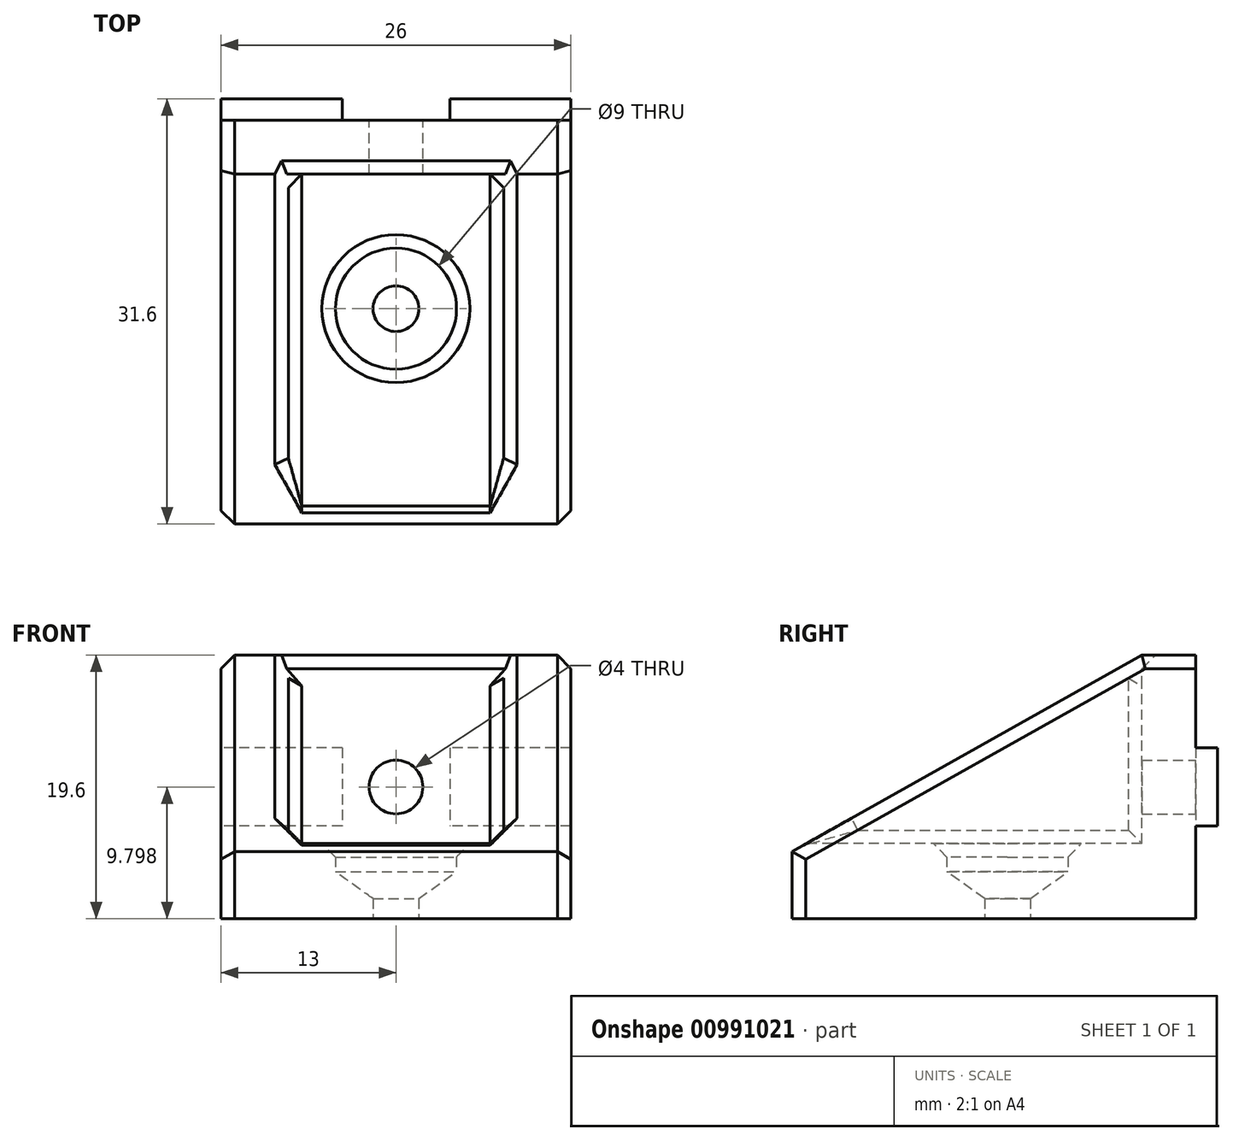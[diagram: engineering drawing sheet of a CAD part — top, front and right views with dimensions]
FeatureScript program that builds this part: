
annotation { "Feature Type Name" : "Feature", "Feature Type Description" : "" }
export const myFeature = defineFeature(function(context is Context, id is Id, definition is map)
    precondition{}
    {
        {
            var Q0;
            Q0=qCreatedBy(makeId("Right.planeOp"),FACE);
            var sketch = newSketch(context, id + "F0", { "sketchPlane" : qUnion([Q0])});
            skLineSegment(sketch, "E0", {"start": v(-34.07, -18.6) * mm, "end": v(-4.07, -18.6) * mm});
            skLineSegment(sketch, "E1", {"start": v(-4.07, -18.6) * mm, "end": v(-4.07, -11.7) * mm});
            skLineSegment(sketch, "E2", {"start": v(-4.07, -11.7) * mm, "end": v(-2.47, -11.7) * mm});
            skLineSegment(sketch, "E3", {"start": v(-2.47, -11.7) * mm, "end": v(-2.47, -5.9) * mm});
            skLineSegment(sketch, "E4", {"start": v(-2.47, -5.9) * mm, "end": v(-4.07, -5.9) * mm});
            skLineSegment(sketch, "E5", {"start": v(-4.07, -5.9) * mm, "end": v(-4.07, 1) * mm});
            skLineSegment(sketch, "E6", {"start": v(-4.07, 1) * mm, "end": v(-8.07, 1) * mm});
            skLineSegment(sketch, "E7", {"start": v(-8.07, 1) * mm, "end": v(-34.07, -13.6) * mm});
            skLineSegment(sketch, "E8", {"start": v(-34.07, -13.6) * mm, "end": v(-34.07, -18.6) * mm});
            skSolve(sketch);
        }
        {
            var Q0;
            Q0=makeQuery(id+"F0.imprint","IMPRINT",FACE,{"disambiguationData":[TD([[makeQuery(id+"F0.imprint","IMPRINT",EDGE,{"derivedFrom":sQuery(id+"F0.wireOp",EDGE,"E0")}),1.0]])]});
            var Q1;
            Q1 = qSketchRegion(id + "F2", true);
            extrude(context, id + "F1", {"entities" : qUnion([Q0, Q1]), "depth" : 26 * mm, "offsetDistance" : 25 * mm});
        }
        {
            var Q0;
            Q0=makeQuery(id+"F1.opExtrude","SWEPT_FACE",FACE,{"disambiguationData":[OSD([sQuery(id+"F0.wireOp",EDGE,"E3")])]});
            var sketch = newSketch(context, id + "F2", { "sketchPlane" : qUnion([Q0])});
            skLineSegment(sketch, "E9", {"start": v(-13, -5.9) * mm, "end": v(-13, -11.7) * mm, "construction": true});
            skCircle(sketch, "E10", {"center": v(-13, -8.8) * mm, "radius": 2 * mm});
            skSolve(sketch);
        }
        {
            var Q0;
            Q0=makeQuery(id+"F2.imprint","IMPRINT",FACE,{"disambiguationData":[TD([[makeQuery(id+"F2.imprint","IMPRINT",EDGE,{"derivedFrom":sQuery(id+"F2.wireOp",EDGE,"E10")}),1.0]])]});
            extrude(context, id + "F3", {"entities" : qUnion([Q0]), "operationType" : NewBodyOperationType.REMOVE, "endBound" : BoundingType.UP_TO_NEXT, "oppositeDirection" : true, "depth" : 25 * mm, "offsetDistance" : 25 * mm});
        }
        {
            var Q0;
            Q0=makeQuery(id+"F1.opExtrude","SWEPT_FACE",FACE,{"disambiguationData":[OSD([sQuery(id+"F0.wireOp",EDGE,"E6")])]});
            var sketch = newSketch(context, id + "F4", { "sketchPlane" : qUnion([Q0])});
            skLineSegment(sketch, "E11", {"start": v(13, -8.07) * mm, "end": v(13, -33.07) * mm, "construction": true});
            skLineSegment(sketch, "E12.bottom", {"start": v(5, -8.07) * mm, "end": v(21, -8.07) * mm});
            skLineSegment(sketch, "E12.top", {"start": v(5, -33.07) * mm, "end": v(21, -33.07) * mm});
            skLineSegment(sketch, "E12.left", {"start": v(5, -8.07) * mm, "end": v(5, -33.07) * mm});
            skLineSegment(sketch, "E12.right", {"start": v(21, -8.07) * mm, "end": v(21, -33.07) * mm});
            skSolve(sketch);
        }
        {
            var Q0;
            Q0=makeQuery(id+"F4.imprint","IMPRINT",FACE,{"disambiguationData":[TD([[makeQuery(id+"F4.imprint","IMPRINT",EDGE,{"derivedFrom":sQuery(id+"F4.wireOp",EDGE,"E12.bottom")}),1.0]])]});
            extrude(context, id + "F5", {"entities" : qUnion([Q0]), "operationType" : NewBodyOperationType.REMOVE, "oppositeDirection" : true, "depth" : 14 * mm, "offsetDistance" : 25 * mm});
        }
        {
            var Q0;
            Q0=makeQuery(id+"F1.opExtrude","SWEPT_FACE",FACE,{"disambiguationData":[OSD([sQuery(id+"F0.wireOp",EDGE,"E3")])]});
            var sketch = newSketch(context, id + "F6", { "sketchPlane" : qUnion([Q0])});
            skLineSegment(sketch, "E13", {"start": v(-13, -5.9) * mm, "end": v(-13, -11.7) * mm, "construction": true});
            skLineSegment(sketch, "E14", {"start": v(-17, -5.9) * mm, "end": v(-17, -11.7) * mm});
            skLineSegment(sketch, "E15.MirrorCS", {"start": v(-9, -5.9) * mm, "end": v(-9, -11.7) * mm});
            skSolve(sketch);
        }
        {
            var Q0;
            {var subQ0=sQuery(id+"F6.wireOp",EDGE,"E14");Q0=makeQuery(id+"F6.imprint","IMPRINT",FACE,{"disambiguationData":[TD([[makeQuery(id+"F6.imprint","IMPRINT",EDGE,{"derivedFrom":subQ0}),1.0]])]});}
            var Q1;
            Q1=makeQuery(id+"F1.opExtrude","SWEPT_FACE",FACE,{"disambiguationData":[OSD([sQuery(id+"F0.wireOp",EDGE,"E5")])]});
            extrude(context, id + "F7", {"entities" : qUnion([Q0]), "operationType" : NewBodyOperationType.REMOVE, "endBound" : BoundingType.UP_TO_SURFACE, "oppositeDirection" : true, "depth" : 25 * mm, "endBoundEntityFace" : qUnion([Q1]), "offsetDistance" : 25 * mm});
        }
        {
            var Q0;
            Q0=makeQuery(id+"F5.boolean.opBoolean","MERGE",EDGE,{"derivedFrom":[makeQuery(id+"F1.opExtrude","SWEPT_EDGE",EDGE,{"disambiguationData":[OSD([sQuery(id+"F0.wireOp",EDGE,"E6"),sQuery(id+"F0.wireOp",EDGE,"E7")])]})],"fromTools":[makeQuery(id+"F5.opExtrude","CAP_EDGE",EDGE,{"disambiguationData":[OSD([sQuery(id+"F4.wireOp",EDGE,"E12.bottom")])],"isStart":true})]});
            cPoint(context, id + "F8", {"entities" : qUnion([Q0]), "parameter" : 0.5});
        }
        {
            var Q0;
            Q0=makeQuery(id+"F5.boolean.opBoolean","INTERSECT",EDGE,{"derivedFrom":[makeQuery(id+"F1.opExtrude","SWEPT_FACE",FACE,{"disambiguationData":[OSD([sQuery(id+"F0.wireOp",EDGE,"E7")])]}),makeQuery(id+"F5.opExtrude","CAP_FACE",FACE,{"disambiguationData":[OSD([sQuery(id+"F4.wireOp",EDGE,"E12.bottom"),sQuery(id+"F4.wireOp",EDGE,"E12.top"),sQuery(id+"F4.wireOp",EDGE,"E12.left"),sQuery(id+"F4.wireOp",EDGE,"E12.right")])],"isStart":false})]});
            cPoint(context, id + "F9", {"entities" : qUnion([Q0]), "parameter" : 0.5});
        }
        {
            var Q0;
            Q0=makeQuery(id+"F5.boolean.opBoolean","COPY",EDGE,{"derivedFrom":makeQuery(id+"F5.opExtrude","CAP_EDGE",EDGE,{"disambiguationData":[OSD([sQuery(id+"F4.wireOp",EDGE,"E12.bottom")])],"isStart":false})});
            cPoint(context, id + "F10", {"entities" : qUnion([Q0]), "parameter" : 0.5});
        }
        {
            var Q0;
            Q0 = qCreatedBy(id + "F8" ,VERTEX);
            var Q1;
            Q1 = qCreatedBy(id + "F9" ,VERTEX);
            var Q2;
            Q2 = qCreatedBy(id + "F10" ,VERTEX);
            cPlane(context, id + "F11", {"entities" : qUnion([Q0, Q1, Q2]), "cplaneType" : CPlaneType.THREE_POINT, "offset" : 25 * mm, "width" : 150 * mm, "height" : 150 * mm});
        }
        {
            var Q0;
            Q0=qCreatedBy(id+"F11.planeOp",FACE);
            var sketch = newSketch(context, id + "F12", { "sketchPlane" : qUnion([Q0])});
            skLineSegment(sketch, "E16", {"start": v(18.07, -2.45) * mm, "end": v(18.07, -17) * mm, "construction": true});
            skLineSegment(sketch, "E17", {"start": v(8.07, -17) * mm, "end": v(18.07, -17) * mm, "construction": true});
            skLineSegment(sketch, "E18", {"start": v(18.07, -10.1) * mm, "end": v(22.57, -10.1) * mm});
            skLineSegment(sketch, "E19", {"start": v(22.57, -10.1) * mm, "end": v(22.57, -15.1) * mm});
            skLineSegment(sketch, "E20", {"start": v(22.57, -15.1) * mm, "end": v(19.77, -17.1) * mm});
            skLineSegment(sketch, "E21", {"start": v(19.77, -17.1) * mm, "end": v(19.77, -22.1) * mm});
            skLineSegment(sketch, "E22", {"start": v(19.77, -22.1) * mm, "end": v(18.07, -22.1) * mm});
            skLineSegment(sketch, "E23", {"start": v(18.07, -10.1) * mm, "end": v(18.07, -22.1) * mm});
            skLineSegment(sketch, "E24", {"start": v(18.07, -10.1) * mm, "end": v(13.57, -10.1) * mm, "construction": true});
            skLineSegment(sketch, "E25", {"start": v(13.57, -10.1) * mm, "end": v(13.57, -15.1) * mm, "construction": true});
            skLineSegment(sketch, "E26", {"start": v(13.57, -15.1) * mm, "end": v(16.37, -17.1) * mm, "construction": true});
            skLineSegment(sketch, "E27", {"start": v(16.37, -17.1) * mm, "end": v(16.37, -22.1) * mm, "construction": true});
            skLineSegment(sketch, "E28", {"start": v(16.37, -22.1) * mm, "end": v(18.07, -22.1) * mm, "construction": true});
            skSolve(sketch);
        }
        {
            var Q0;
            Q0 = qSketchRegion(id + "F12", true);
            var Q1;
            Q1=sQuery(id+"F12.wireOp",EDGE,"E16");
            revolve(context, id + "F13", {"operationType" : NewBodyOperationType.REMOVE, "surfaceOperationType" : NewSurfaceOperationType.NEW, "entities" : qUnion([Q0]), "axis" : qUnion([Q1]), "revolveType" : RevolveType.FULL, "oppositeDirection" : true});
        }
        {
            var Q0;
            Q0=makeQuery(id+"F1.opExtrude","CAP_EDGE",EDGE,{"disambiguationData":[OSD([sQuery(id+"F0.wireOp",EDGE,"E6")])],"isStart":true});
            var Q1;
            Q1=makeQuery(id+"F1.opExtrude","CAP_EDGE",EDGE,{"disambiguationData":[OSD([sQuery(id+"F0.wireOp",EDGE,"E7")])],"isStart":true});
            var Q2;
            Q2=makeQuery(id+"F5.boolean.opBoolean","INTERSECT",EDGE,{"derivedFrom":[makeQuery(id+"F1.opExtrude","SWEPT_FACE",FACE,{"disambiguationData":[OSD([sQuery(id+"F0.wireOp",EDGE,"E7")])]}),makeQuery(id+"F5.opExtrude","SWEPT_FACE",FACE,{"disambiguationData":[OSD([sQuery(id+"F4.wireOp",EDGE,"E12.left")])]})]});
            var Q3;
            Q3=makeQuery(id+"F5.boolean.opBoolean","INTERSECT",EDGE,{"derivedFrom":[makeQuery(id+"F1.opExtrude","SWEPT_FACE",FACE,{"disambiguationData":[OSD([sQuery(id+"F0.wireOp",EDGE,"E7")])]}),makeQuery(id+"F5.opExtrude","SWEPT_FACE",FACE,{"disambiguationData":[OSD([sQuery(id+"F4.wireOp",EDGE,"E12.right")])]})]});
            var Q4;
            Q4=makeQuery(id+"F1.opExtrude","CAP_EDGE",EDGE,{"disambiguationData":[OSD([sQuery(id+"F0.wireOp",EDGE,"E7")])],"isStart":false});
            var Q5;
            Q5=makeQuery(id+"F1.opExtrude","CAP_EDGE",EDGE,{"disambiguationData":[OSD([sQuery(id+"F0.wireOp",EDGE,"E6")])],"isStart":false});
            var Q6;
            Q6=makeQuery(id+"F1.opExtrude","CAP_EDGE",EDGE,{"disambiguationData":[OSD([sQuery(id+"F0.wireOp",EDGE,"E8")])],"isStart":true});
            var Q7;
            Q7=makeQuery(id+"F1.opExtrude","CAP_EDGE",EDGE,{"disambiguationData":[OSD([sQuery(id+"F0.wireOp",EDGE,"E8")])],"isStart":false});
            var Q8;
            Q8=makeQuery(id+"F13.boolean.opBoolean","INTERSECT",EDGE,{"derivedFrom":[makeQuery(id+"F5.boolean.opBoolean","COPY",FACE,{"derivedFrom":makeQuery(id+"F5.opExtrude","CAP_FACE",FACE,{"disambiguationData":[OSD([sQuery(id+"F4.wireOp",EDGE,"E12.bottom"),sQuery(id+"F4.wireOp",EDGE,"E12.top"),sQuery(id+"F4.wireOp",EDGE,"E12.left"),sQuery(id+"F4.wireOp",EDGE,"E12.right")])],"isStart":false})}),makeQuery(id+"F13.opRevolve","SWEPT_FACE",FACE,{"disambiguationData":[OSD([sQuery(id+"F12.wireOp",EDGE,"E19")])]})]});
            var Q9;
            Q9=makeQuery(id+"F5.boolean.opBoolean","COPY",EDGE,{"derivedFrom":makeQuery(id+"F5.opExtrude","CAP_EDGE",EDGE,{"disambiguationData":[OSD([sQuery(id+"F4.wireOp",EDGE,"E12.right")])],"isStart":false})});
            var Q10;
            Q10=makeQuery(id+"F5.boolean.opBoolean","COPY",EDGE,{"derivedFrom":makeQuery(id+"F5.opExtrude","CAP_EDGE",EDGE,{"disambiguationData":[OSD([sQuery(id+"F4.wireOp",EDGE,"E12.left")])],"isStart":false})});
            chamfer(context, id + "F14", {"entities" : qUnion([Q0, Q1, Q2, Q3, Q4, Q5, Q6, Q7, Q8, Q9, Q10]), "width" : 1 * mm, "tangentPropagation" : true});
        }
        {
            var Q0;
            {var subQ0=sQuery(id+"F0.wireOp",EDGE,"E7");var subQ2=sQuery(id+"F0.wireOp",EDGE,"E6");var subQ4=sQuery(id+"F4.wireOp",EDGE,"E12.bottom");var subQ13=makeQuery(id+"F1.opExtrude","SWEPT_EDGE",EDGE,{"disambiguationData":[OSD([subQ2,subQ0])]});Q0=makeQuery(id+"F14.opChamfer","MERGE",EDGE,{"derivedFrom":[makeQuery(id+"F5.boolean.opBoolean","MERGE",EDGE,{"derivedFrom":[subQ13],"fromTools":[makeQuery(id+"F5.opExtrude","CAP_EDGE",EDGE,{"disambiguationData":[OSD([subQ4])],"isStart":true})]}),makeQuery(id+"F5.boolean.opBoolean","SPLIT",EDGE,{"disambiguationData":[TD([makeQuery(id+"F5.opExtrude","SWEPT_FACE",FACE,{"disambiguationData":[OSD([sQuery(id+"F4.wireOp",EDGE,"E12.left")])]})])],"derivedFrom":subQ13}),makeQuery(id+"F5.boolean.opBoolean","SPLIT",EDGE,{"disambiguationData":[TD([makeQuery(id+"F5.opExtrude","SWEPT_FACE",FACE,{"disambiguationData":[OSD([sQuery(id+"F4.wireOp",EDGE,"E12.right")])]})])],"derivedFrom":subQ13})]});}
            var Q1;
            Q1=makeQuery(id+"F5.boolean.opBoolean","COPY",EDGE,{"derivedFrom":makeQuery(id+"F5.opExtrude","SWEPT_EDGE",EDGE,{"disambiguationData":[OSD([sQuery(id+"F0.wireOp",EDGE,"E6"),sQuery(id+"F0.wireOp",EDGE,"E7"),sQuery(id+"F4.wireOp",EDGE,"E12.bottom"),sQuery(id+"F4.wireOp",EDGE,"E12.left")])]})});
            var Q2;
            Q2=makeQuery(id+"F5.boolean.opBoolean","COPY",EDGE,{"derivedFrom":makeQuery(id+"F5.opExtrude","SWEPT_EDGE",EDGE,{"disambiguationData":[OSD([sQuery(id+"F0.wireOp",EDGE,"E6"),sQuery(id+"F0.wireOp",EDGE,"E7"),sQuery(id+"F4.wireOp",EDGE,"E12.bottom"),sQuery(id+"F4.wireOp",EDGE,"E12.right")])]})});
            chamfer(context, id + "F15", {"entities" : qUnion([Q0, Q1, Q2]), "width" : 1 * mm, "tangentPropagation" : true});
        }
    });
